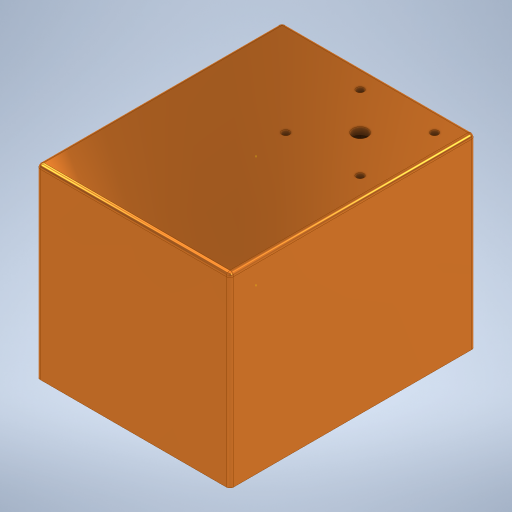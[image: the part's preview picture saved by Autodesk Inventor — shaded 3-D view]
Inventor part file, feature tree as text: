
AUTODESK INVENTOR PART (.ipt)
format: ipt  version: 2023 (Build 270158000, 158)  size: 381,440 bytes
history: native  units: mm
features: extrude x13, sketch x13, fillet x3, chamfer x1, projected_geometry x1
ambient origin geometry x8: Origin, YZ Plane, XZ Plane, XY Plane, X Axis, Y Axis, Z Axis, Center Point
bodies: Solid1 (feature_tree)
feature tree (31):
  extrude  "Extrusion1"  Depth=330.0mm
  extrude  "Extrusion2"  Depth=10.0mm
  fillet  "Fillet1"  Radius=10.0mm
  extrude  "Extrusion3"  Depth=5.0mm
  extrude  "Extrusion4"  Depth=10.0mm
  extrude  "Extrusion5"  Depth=10.0mm
  extrude  "Extrusion6"  Depth=22.5mm
  sketch  "Sketch8"  dims[d14=100.0mm d15=22.5mm]
  extrude  "Extrusion7"  Depth=8.0mm TaperAngle=0.0deg
  fillet  "Fillet2"  Radius=20.0mm
  sketch  "Sketch10"  dims[d16=22.5mm d17=8.0mm d18=0.0mm d19=20.0mm]
  extrude  "Extrusion8"  Depth=50.0mm
  extrude  "Extrusion9"  Depth=70.0mm
  extrude  "Extrusion11"  Depth=150.0mm TaperAngle=0.0deg
  extrude  "Extrusion12"  Depth=35.0mm
  chamfer  "Chamfer2"  Distance=150.0mm
  extrude  "Extrusion13"  Depth=5.0mm
  extrude  "Extrusion14"  Depth=15.0mm
  fillet  "Fillet3"  Radius=14.5mm
  sketch  "Sketch1"  dims[d0=260.0mm d1=330.0mm]
  sketch  "Sketch2"  dims[d2=250.0mm d3=0.0mm d4=10.0mm d5=10.0mm]
  sketch  "Sketch3"  dims[d6=240.0mm d7=0.0mm d8=5.0mm]
  sketch  "Sketch4"  dims[d9=10.0mm d10=10.0mm]
  sketch  "Sketch7"  dims[d11=10.0mm d12=10.0mm d13=100.0mm]
  sketch  "Sketch11"  dims[d20=50.0mm d21=50.0mm]
  sketch  "Sketch12"  dims[d22=8.0mm d23=0.0mm d24=70.0mm]
  sketch  "Sketch15"  dims[d25=60.0mm d26=150.0mm d27=0.0mm]
  sketch  "Sketch17"  dims[d28=65.0mm d29=35.0mm d30=150.0mm d31=0.0mm]
  sketch  "Sketch18"  dims[d32=5.0mm d33=5.0mm]
  sketch  "Sketch19"  dims[d39=150.0mm d40=0.0mm d43=14.5mm d44=14.5mm d45=15.0mm d46=1.0mm d47=1.0mm d48=1.0mm d49=1.0mm d50=5.0mm d51=0.0mm d52=70.0mm d53=150.0mm d54=60.0mm d55=130.0mm d56=0.0mm d57=0.0mm d68=50.0mm d69=0.0mm d70=0.5mm d71=0.5mm d72=0.5mm d73=0.5mm d74=5.0mm d75=0.0mm d76=0.2mm d77=2.0mm d78=45.0deg d79=100.0mm d80=30.0mm d82=150.0mm d83=0.0mm d84=5.0mm d85=5.0mm d87=5.0mm d88=140.0mm d89=0.0mm d90=5.0mm d91=15.0mm]
  projected_geometry  "Projected Loop1"
